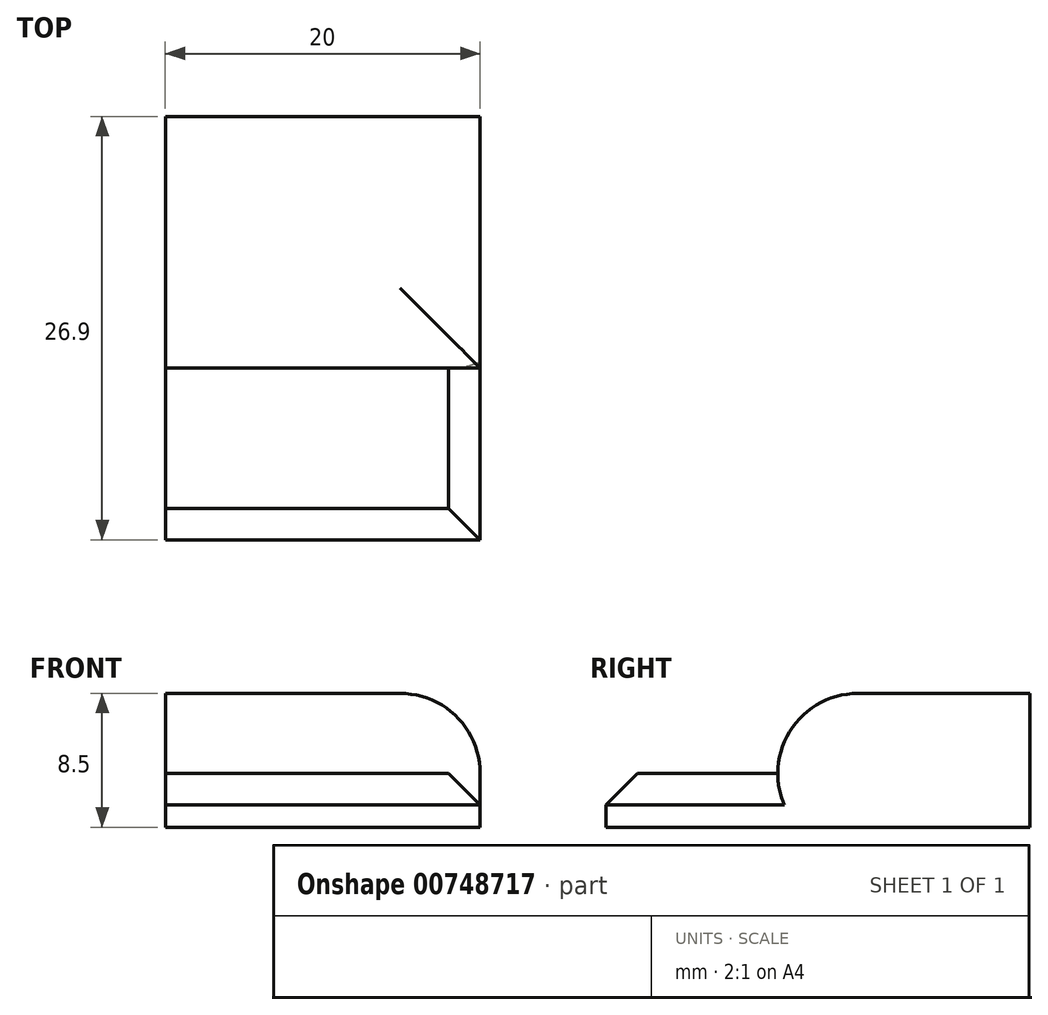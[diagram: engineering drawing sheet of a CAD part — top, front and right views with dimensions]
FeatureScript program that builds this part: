
annotation { "Feature Type Name" : "Feature", "Feature Type Description" : "" }
export const myFeature = defineFeature(function(context is Context, id is Id, definition is map)
    precondition{}
    {
        {
            var Q0;
            Q0=qCreatedBy(makeId("Top.planeOp"),FACE);
            var sketch = newSketch(context, id + "F0", { "sketchPlane" : qUnion([Q0])});
            skLineSegment(sketch, "E0.bottom", {"start": v(-3.83, 7.76) * mm, "end": v(16.17, 7.76) * mm});
            skLineSegment(sketch, "E0.top", {"start": v(-3.83, -8.24) * mm, "end": v(16.17, -8.24) * mm});
            skLineSegment(sketch, "E0.left", {"start": v(-3.83, 7.76) * mm, "end": v(-3.83, -8.24) * mm});
            skLineSegment(sketch, "E0.right", {"start": v(16.17, 7.76) * mm, "end": v(16.17, -8.24) * mm});
            skArc(sketch, "E1", {"start": v(16.17, 7.76) * mm, "mid": v(2.33, 4.57) * mm, "end": v(-3.83, -8.24) * mm});
            skSolve(sketch);
        }
        {
            var Q0;
            Q0=makeQuery(id+"F0.imprint","IMPRINT",FACE,{"disambiguationData":[TD([[makeQuery(id+"F0.imprint","IMPRINT",EDGE,{"derivedFrom":sQuery(id+"F0.wireOp",EDGE,"E0.bottom")}),-1.0]])]});
            var Q1;
            {var subQ4=sQuery(id+"F0.wireOp",EDGE,"E0.top");Q1=makeQuery(id+"F0.imprint","IMPRINT",FACE,{"disambiguationData":[TD([[makeQuery(id+"F0.imprint","IMPRINT",EDGE,{"derivedFrom":subQ4}),1.0]])]});}
            extrude(context, id + "F1", {"entities" : qUnion([Q0, Q1]), "depth" : 8.5 * mm, "offsetDistance" : 25.4 * mm});
        }
        {
            var Q0;
            Q0=makeQuery(id+"F1.opExtrude","CAP_EDGE",EDGE,{"disambiguationData":[OSD([sQuery(id+"F0.wireOp",EDGE,"E0.right")])],"isStart":false});
            var Q1;
            Q1=makeQuery(id+"F1.opExtrude","CAP_EDGE",EDGE,{"disambiguationData":[OSD([sQuery(id+"F0.wireOp",EDGE,"E0.top")])],"isStart":false});
            fillet(context, id + "F2", {"entities" : qUnion([Q0, Q1]), "tangentPropagation" : true, "radius" : 5.08 * mm, "defaultsChanged" : false, "vertexSettings" : [], "allowEdgeOverflow" : false});
        }
        {
            var Q0;
            Q0=makeQuery(id+"F1.opExtrude","SWEPT_FACE",FACE,{"disambiguationData":[OSD([sQuery(id+"F0.wireOp",EDGE,"E0.top")])]});
            extrude(context, id + "F3", {"entities" : qUnion([Q0]), "operationType" : NewBodyOperationType.ADD, "depth" : 10.9 * mm, "offsetDistance" : 25.4 * mm});
        }
        {
            var Q0;
            {var subQ0=sQuery(id+"F0.wireOp",EDGE,"E0.top");Q0=makeQuery(id+"F3.opExtrude","CAP_EDGE",EDGE,{"disambiguationData":[OSD([subQ0]),TDD([makeQuery(id+"F2.opFillet","BLEND_EDGE",EDGE,{"blendedFrom":[makeQuery(id+"F1.opExtrude","CAP_EDGE",EDGE,{"disambiguationData":[OSD([subQ0])],"isStart":false}),makeQuery(id+"F1.opExtrude","SWEPT_FACE",FACE,{"disambiguationData":[OSD([subQ0])]})],"blendedInto":[makeQuery(id+"F1.opExtrude","SWEPT_FACE",FACE,{"disambiguationData":[OSD([subQ0])]})]})])],"isStart":false});}
            chamfer(context, id + "F4", {"entities" : qUnion([Q0]), "width" : 2 * mm, "tangentPropagation" : true});
        }
        {
            var Q0;
            {var subQ0=sQuery(id+"F0.wireOp",EDGE,"E0.right");var subQ1=sQuery(id+"F0.wireOp",EDGE,"E0.top");Q0=makeQuery(id+"F3.opExtrude","SWEPT_EDGE",EDGE,{"disambiguationData":[OSD([subQ1,subQ0]),TDD([makeQuery(id+"F2.opFillet","BLEND_VERTEX",VERTEX,{"blendedFrom":[makeQuery(id+"F1.opExtrude","CAP_EDGE",EDGE,{"disambiguationData":[OSD([subQ1])],"isStart":false}),makeQuery(id+"F1.opExtrude","CAP_EDGE",EDGE,{"disambiguationData":[OSD([subQ0])],"isStart":false}),makeQuery(id+"F1.opExtrude","SWEPT_FACE",FACE,{"disambiguationData":[OSD([subQ1])]}),makeQuery(id+"F1.opExtrude","SWEPT_FACE",FACE,{"disambiguationData":[OSD([subQ0])]})],"blendedInto":[makeQuery(id+"F1.opExtrude","SWEPT_FACE",FACE,{"disambiguationData":[OSD([subQ1])]}),makeQuery(id+"F1.opExtrude","SWEPT_FACE",FACE,{"disambiguationData":[OSD([subQ0])]})]})])]});}
            chamfer(context, id + "F5", {"entities" : qUnion([Q0]), "width" : 2 * mm, "tangentPropagation" : true});
        }
    });
